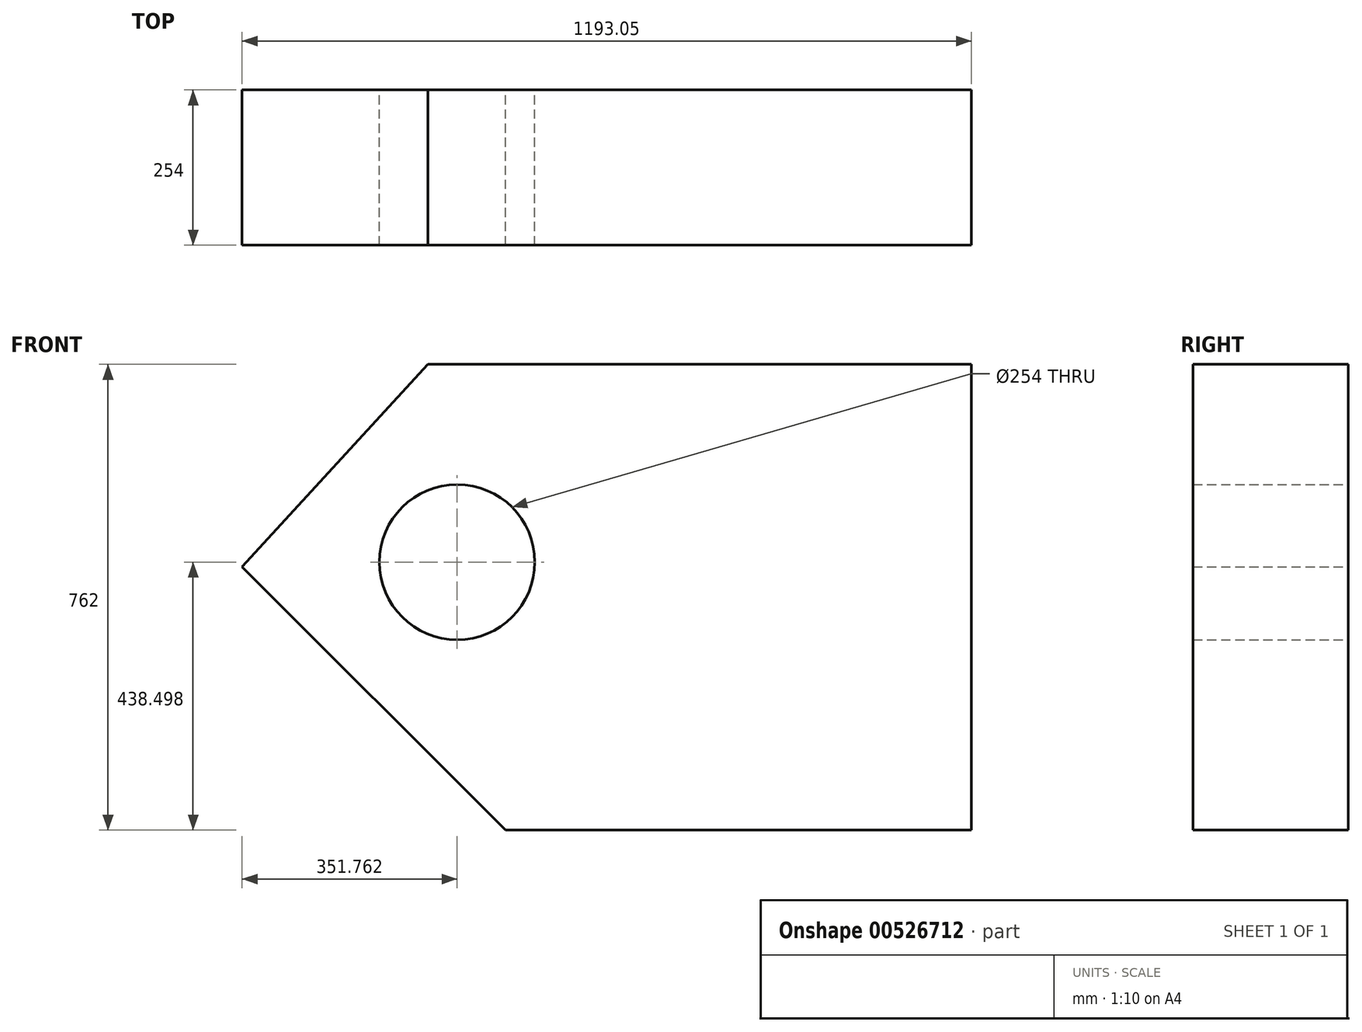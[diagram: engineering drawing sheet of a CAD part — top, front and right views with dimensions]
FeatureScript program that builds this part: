
annotation { "Feature Type Name" : "Feature", "Feature Type Description" : "" }
export const myFeature = defineFeature(function(context is Context, id is Id, definition is map)
    precondition{}
    {
        {
            var Q0;
            Q0=qCreatedBy(makeId("Front.planeOp"),FACE);
            var sketch = newSketch(context, id + "F0", { "sketchPlane" : qUnion([Q0])});
            skLineSegment(sketch, "E0", {"start": v(0, 0) * mm, "end": v(-762, 0) * mm});
            skLineSegment(sketch, "E1", {"start": v(-762, 0) * mm, "end": v(-1193.05, 431.05) * mm});
            skLineSegment(sketch, "E2", {"start": v(0, 0) * mm, "end": v(0, 762) * mm});
            skLineSegment(sketch, "E3", {"start": v(0, 762) * mm, "end": v(-889, 762) * mm});
            skLineSegment(sketch, "E4", {"start": v(-889, 762) * mm, "end": v(-1193.05, 431.05) * mm});
            skCircle(sketch, "E5", {"center": v(-841.29, 438.5) * mm, "radius": 127 * mm});
            skSolve(sketch);
        }
        {
            var Q0;
            Q0 = qSketchRegion(id + "F0", true);
            extrude(context, id + "F1", {"entities" : qUnion([Q0]), "depth" : 254 * mm, "offsetDistance" : 25.4 * mm});
        }
    });
